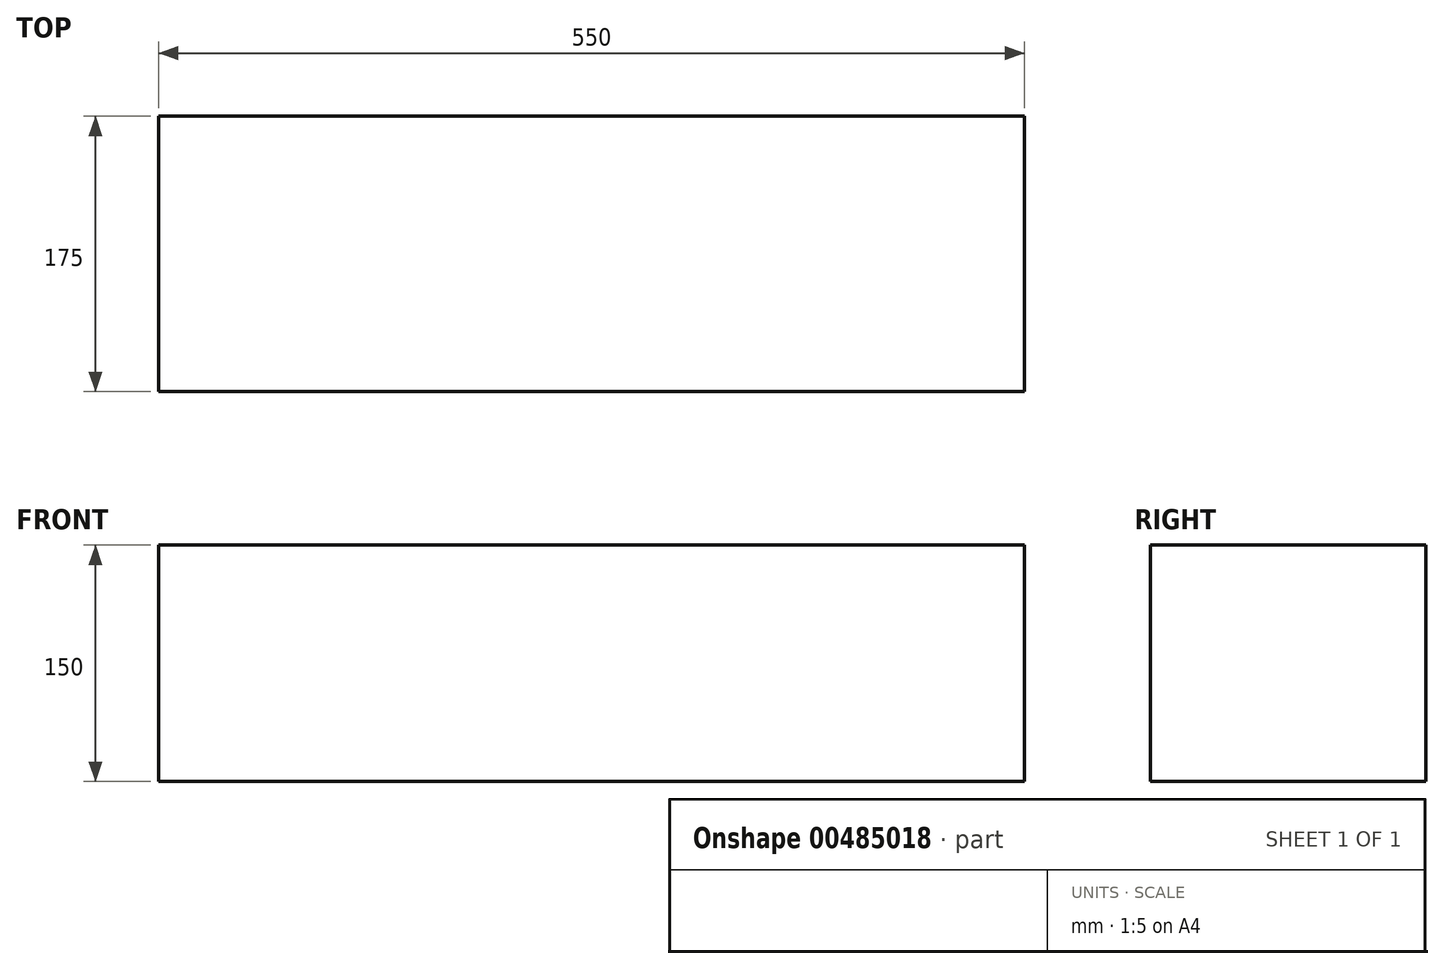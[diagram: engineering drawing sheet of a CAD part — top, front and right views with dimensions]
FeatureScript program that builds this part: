
annotation { "Feature Type Name" : "Feature", "Feature Type Description" : "" }
export const myFeature = defineFeature(function(context is Context, id is Id, definition is map)
    precondition{}
    {
        {
            var Q0;
            Q0=qCreatedBy(makeId("Top.planeOp"),FACE);
            var sketch = newSketch(context, id + "F0", { "sketchPlane" : qUnion([Q0])});
            skLineSegment(sketch, "E0.bottom", {"start": v(275, 87.5) * mm, "end": v(-275, 87.5) * mm});
            skLineSegment(sketch, "E0.top", {"start": v(275, -87.5) * mm, "end": v(-275, -87.5) * mm});
            skLineSegment(sketch, "E0.left", {"start": v(275, 87.5) * mm, "end": v(275, -87.5) * mm});
            skLineSegment(sketch, "E0.right", {"start": v(-275, 87.5) * mm, "end": v(-275, -87.5) * mm});
            skPoint(sketch, "E0.middle", {"position": v(0, 0) * mm});
            skSolve(sketch);
        }
        {
            var Q0;
            Q0=makeQuery(id+"F0.imprint","IMPRINT",FACE,{"disambiguationData":[TD([[makeQuery(id+"F0.imprint","IMPRINT",EDGE,{"derivedFrom":sQuery(id+"F0.wireOp",EDGE,"E0.bottom")}),1.0]])]});
            extrude(context, id + "F1", {"entities" : qUnion([Q0]), "depth" : 150 * mm, "offsetDistance" : 25 * mm});
        }
    });
